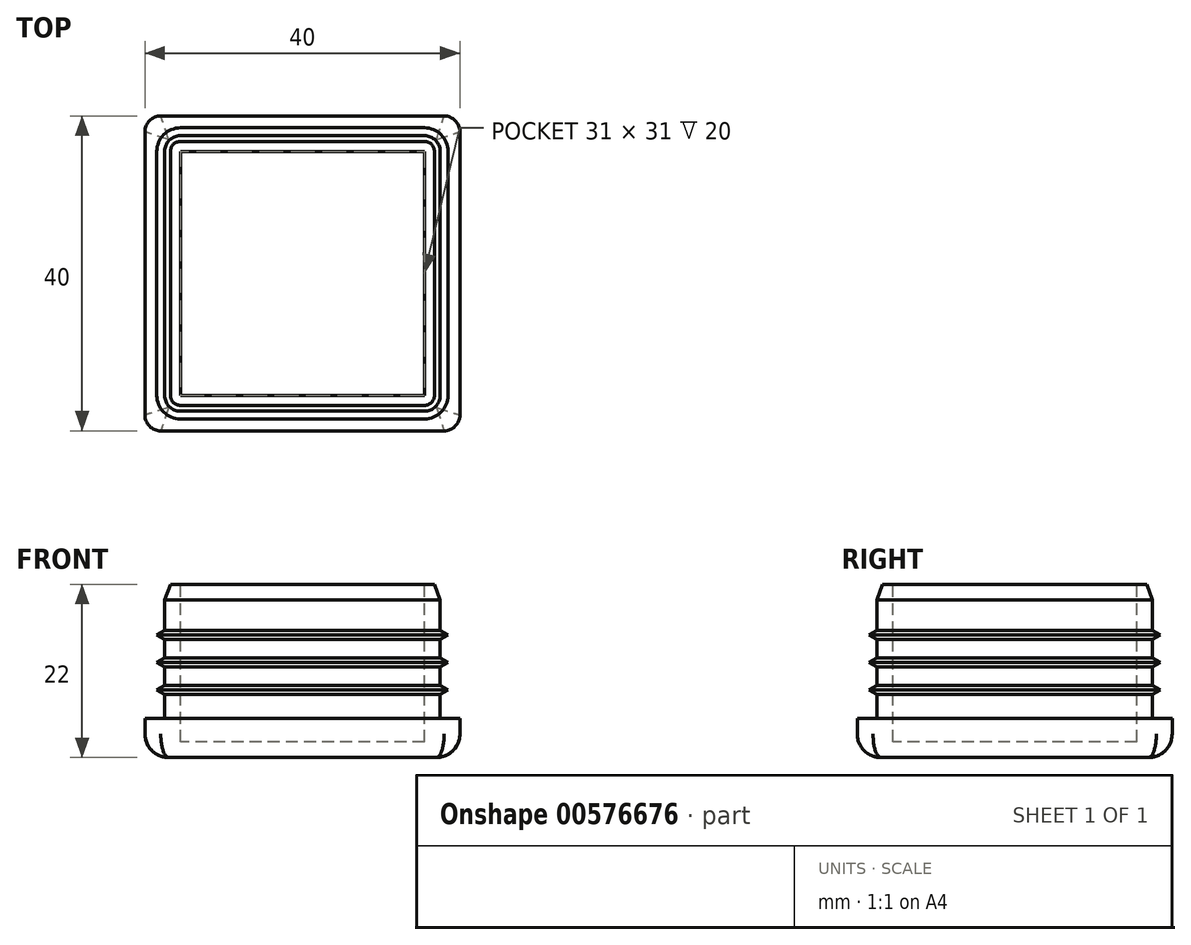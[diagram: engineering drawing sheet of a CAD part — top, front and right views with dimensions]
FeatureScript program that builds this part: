
annotation { "Feature Type Name" : "Feature", "Feature Type Description" : "" }
export const myFeature = defineFeature(function(context is Context, id is Id, definition is map)
    precondition{}
    {
        {
            var Q0;
            Q0=qCreatedBy(makeId("Top.planeOp"),FACE);
            var sketch = newSketch(context, id + "F0", { "sketchPlane" : qUnion([Q0])});
            skLineSegment(sketch, "E0.bottom", {"start": v(0, 0) * mm, "end": v(40, 0) * mm});
            skLineSegment(sketch, "E0.top", {"start": v(0, 40) * mm, "end": v(40, 40) * mm});
            skLineSegment(sketch, "E0.left", {"start": v(0, 0) * mm, "end": v(0, 40) * mm});
            skLineSegment(sketch, "E0.right", {"start": v(40, 0) * mm, "end": v(40, 40) * mm});
            skSolve(sketch);
        }
        {
            var Q0;
            Q0=makeQuery(id+"F0.imprint","IMPRINT",FACE,{"disambiguationData":[TD([[makeQuery(id+"F0.imprint","IMPRINT",EDGE,{"derivedFrom":sQuery(id+"F0.wireOp",EDGE,"E0.bottom")}),1.0]])]});
            extrude(context, id + "F1", {"entities" : qUnion([Q0]), "depth" : 5 * mm, "offsetDistance" : 25 * mm});
        }
        {
            var Q0;
            Q0=makeQuery(id+"F1.opExtrude","SWEPT_EDGE",EDGE,{"disambiguationData":[OSD([sQuery(id+"F0.wireOp",EDGE,"E0.bottom"),sQuery(id+"F0.wireOp",EDGE,"E0.left")])]});
            var Q1;
            Q1=makeQuery(id+"F1.opExtrude","SWEPT_EDGE",EDGE,{"disambiguationData":[OSD([sQuery(id+"F0.wireOp",EDGE,"E0.top"),sQuery(id+"F0.wireOp",EDGE,"E0.right")])]});
            var Q2;
            Q2=makeQuery(id+"F1.opExtrude","SWEPT_EDGE",EDGE,{"disambiguationData":[OSD([sQuery(id+"F0.wireOp",EDGE,"E0.bottom"),sQuery(id+"F0.wireOp",EDGE,"E0.right")])]});
            var Q3;
            Q3=makeQuery(id+"F1.opExtrude","SWEPT_EDGE",EDGE,{"disambiguationData":[OSD([sQuery(id+"F0.wireOp",EDGE,"E0.top"),sQuery(id+"F0.wireOp",EDGE,"E0.left")])]});
            fillet(context, id + "F2", {"entities" : qUnion([Q0, Q1, Q2, Q3]), "radius" : 2 * mm, "tangentPropagation" : true, "allowEdgeOverflow" : false});
        }
        {
            var Q0;
            Q0=makeQuery(id+"F1.opExtrude","CAP_FACE",FACE,{"disambiguationData":[OSD([sQuery(id+"F0.wireOp",EDGE,"E0.bottom"),sQuery(id+"F0.wireOp",EDGE,"E0.top"),sQuery(id+"F0.wireOp",EDGE,"E0.left"),sQuery(id+"F0.wireOp",EDGE,"E0.right")])],"isStart":true});
            fillet(context, id + "F3", {"entities" : qUnion([Q0]), "radius" : 3 * mm, "tangentPropagation" : true, "allowEdgeOverflow" : false});
        }
        {
            var Q0;
            Q0=makeQuery(id+"F1.opExtrude","CAP_FACE",FACE,{"disambiguationData":[OSD([sQuery(id+"F0.wireOp",EDGE,"E0.bottom"),sQuery(id+"F0.wireOp",EDGE,"E0.top"),sQuery(id+"F0.wireOp",EDGE,"E0.left"),sQuery(id+"F0.wireOp",EDGE,"E0.right")])],"isStart":false});
            var sketch = newSketch(context, id + "F4", { "sketchPlane" : qUnion([Q0])});
            skLineSegment(sketch, "E1.bottom", {"start": v(2.5, 37.5) * mm, "end": v(37.5, 37.5) * mm});
            skLineSegment(sketch, "E1.top", {"start": v(2.5, 2.5) * mm, "end": v(37.5, 2.5) * mm});
            skLineSegment(sketch, "E1.left", {"start": v(2.5, 37.5) * mm, "end": v(2.5, 2.5) * mm});
            skLineSegment(sketch, "E1.right", {"start": v(37.5, 37.5) * mm, "end": v(37.5, 2.5) * mm});
            skSolve(sketch);
        }
        {
            var Q0;
            Q0=makeQuery(id+"F4.imprint","IMPRINT",FACE,{"disambiguationData":[TD([[makeQuery(id+"F4.imprint","IMPRINT",EDGE,{"derivedFrom":sQuery(id+"F4.wireOp",EDGE,"E1.bottom")}),-1.0]])]});
            extrude(context, id + "F5", {"entities" : qUnion([Q0]), "operationType" : NewBodyOperationType.ADD, "depth" : 17 * mm, "offsetDistance" : 25 * mm});
        }
        {
            var Q0;
            Q0=makeQuery(id+"F5.opExtrude","SWEPT_EDGE",EDGE,{"disambiguationData":[OSD([sQuery(id+"F4.wireOp",EDGE,"E1.top"),sQuery(id+"F4.wireOp",EDGE,"E1.right")])]});
            var Q1;
            Q1=makeQuery(id+"F5.opExtrude","SWEPT_EDGE",EDGE,{"disambiguationData":[OSD([sQuery(id+"F4.wireOp",EDGE,"E1.bottom"),sQuery(id+"F4.wireOp",EDGE,"E1.right")])]});
            var Q2;
            Q2=makeQuery(id+"F5.opExtrude","SWEPT_EDGE",EDGE,{"disambiguationData":[OSD([sQuery(id+"F4.wireOp",EDGE,"E1.top"),sQuery(id+"F4.wireOp",EDGE,"E1.left")])]});
            var Q3;
            Q3=makeQuery(id+"F5.opExtrude","SWEPT_EDGE",EDGE,{"disambiguationData":[OSD([sQuery(id+"F4.wireOp",EDGE,"E1.bottom"),sQuery(id+"F4.wireOp",EDGE,"E1.left")])]});
            fillet(context, id + "F6", {"entities" : qUnion([Q0, Q1, Q2, Q3]), "radius" : 2 * mm, "tangentPropagation" : true, "allowEdgeOverflow" : false});
        }
        {
            var Q0;
            Q0=makeQuery(id+"F5.opExtrude","CAP_FACE",FACE,{"disambiguationData":[OSD([sQuery(id+"F4.wireOp",EDGE,"E1.bottom"),sQuery(id+"F4.wireOp",EDGE,"E1.top"),sQuery(id+"F4.wireOp",EDGE,"E1.left"),sQuery(id+"F4.wireOp",EDGE,"E1.right")])],"isStart":false});
            var sketch = newSketch(context, id + "F7", { "sketchPlane" : qUnion([Q0])});
            skLineSegment(sketch, "E2.bottom", {"start": v(4.5, 4.5) * mm, "end": v(35.5, 4.5) * mm});
            skLineSegment(sketch, "E2.top", {"start": v(4.5, 35.5) * mm, "end": v(35.5, 35.5) * mm});
            skLineSegment(sketch, "E2.left", {"start": v(4.5, 4.5) * mm, "end": v(4.5, 35.5) * mm});
            skLineSegment(sketch, "E2.right", {"start": v(35.5, 4.5) * mm, "end": v(35.5, 35.5) * mm});
            skSolve(sketch);
        }
        {
            var Q0;
            Q0=makeQuery(id+"F7.imprint","IMPRINT",FACE,{"disambiguationData":[TD([[makeQuery(id+"F7.imprint","IMPRINT",EDGE,{"derivedFrom":sQuery(id+"F7.wireOp",EDGE,"E2.bottom")}),1.0]])]});
            var Q1;
            Q1=makeQuery(id+"F1.opExtrude","CAP_FACE",FACE,{"disambiguationData":[OSD([sQuery(id+"F0.wireOp",EDGE,"E0.bottom"),sQuery(id+"F0.wireOp",EDGE,"E0.top"),sQuery(id+"F0.wireOp",EDGE,"E0.left"),sQuery(id+"F0.wireOp",EDGE,"E0.right")])],"isStart":true});
            extrude(context, id + "F8", {"entities" : qUnion([Q0]), "operationType" : NewBodyOperationType.REMOVE, "endBound" : BoundingType.UP_TO_SURFACE, "oppositeDirection" : true, "depth" : 20 * mm, "endBoundEntityFace" : qUnion([Q1]), "hasOffset" : true, "offsetDistance" : 2 * mm});
        }
        {
            var Q0;
            Q0=makeQuery(id+"F1.opExtrude","CAP_FACE",FACE,{"disambiguationData":[OSD([sQuery(id+"F0.wireOp",EDGE,"E0.bottom"),sQuery(id+"F0.wireOp",EDGE,"E0.top"),sQuery(id+"F0.wireOp",EDGE,"E0.left"),sQuery(id+"F0.wireOp",EDGE,"E0.right")])],"isStart":false});
            cPlane(context, id + "F9", {"entities" : qUnion([Q0]), "cplaneType" : CPlaneType.OFFSET, "offset" : 3 * mm, "width" : 150 * mm, "height" : 150 * mm});
        }
        {
            var Q0;
            Q0=qCreatedBy(id+"F9.planeOp",FACE);
            var sketch = newSketch(context, id + "F10", { "sketchPlane" : qUnion([Q0])});
            skLineSegment(sketch, "E3", {"start": v(37.5, 4.5) * mm, "end": v(37.5, 35.5) * mm});
            skArc(sketch, "E4", {"start": v(35.5, 2.5) * mm, "mid": v(36.91, 3.09) * mm, "end": v(37.5, 4.5) * mm});
            skLineSegment(sketch, "E5", {"start": v(35.5, 2.5) * mm, "end": v(4.5, 2.5) * mm});
            skLineSegment(sketch, "E6", {"start": v(2.5, 4.5) * mm, "end": v(2.5, 35.5) * mm});
            skArc(sketch, "E7", {"start": v(2.5, 4.5) * mm, "mid": v(3.09, 3.09) * mm, "end": v(4.5, 2.5) * mm});
            skArc(sketch, "E8", {"start": v(4.5, 37.5) * mm, "mid": v(3.09, 36.91) * mm, "end": v(2.5, 35.5) * mm});
            skLineSegment(sketch, "E9", {"start": v(35.5, 37.5) * mm, "end": v(4.5, 37.5) * mm});
            skArc(sketch, "E10", {"start": v(37.5, 35.5) * mm, "mid": v(36.91, 36.91) * mm, "end": v(35.5, 37.5) * mm});
            skSolve(sketch);
        }
        {
            var Q0;
            Q0=sQuery(id+"F10.wireOp",VERTEX,"E7.start");
            var Q1;
            Q1=qCreatedBy(makeId("Front.planeOp"),FACE);
            cPlane(context, id + "F11", {"entities" : qUnion([Q0, Q1]), "cplaneType" : CPlaneType.PLANE_POINT, "offset" : 25 * mm, "oppositeDirection" : true, "width" : 150 * mm, "height" : 150 * mm});
        }
        {
            var Q0;
            Q0=qCreatedBy(id+"F11.planeOp",FACE);
            var sketch = newSketch(context, id + "F12", { "sketchPlane" : qUnion([Q0])});
            skLineSegment(sketch, "E11", {"start": v(2.5, 16.15) * mm, "end": v(2.5, 22) * mm, "construction": true});
            skLineSegment(sketch, "E12", {"start": v(2.5, 8.58) * mm, "end": v(10.18, 8.58) * mm, "construction": true});
            skLineSegment(sketch, "E13.0", {"start": v(1.5, -0.73) * mm, "end": v(1.5, 8.58) * mm, "construction": true});
            skLineSegment(sketch, "E14", {"start": v(1.5, 8.58) * mm, "end": v(2.5, 9.15) * mm});
            skLineSegment(sketch, "E15", {"start": v(2.5, 9.15) * mm, "end": v(2.5, 8) * mm, "construction": true});
            skLineSegment(sketch, "E16", {"start": v(2.5, 8) * mm, "end": v(1.5, 8.58) * mm});
            skLineSegment(sketch, "E17.0.1.0", {"start": v(2.5, 11.5) * mm, "end": v(1.5, 12.08) * mm});
            skLineSegment(sketch, "E17.0.1.1", {"start": v(2.5, 12.65) * mm, "end": v(2.5, 11.5) * mm, "construction": true});
            skLineSegment(sketch, "E17.0.1.2", {"start": v(1.5, 12.08) * mm, "end": v(2.5, 12.65) * mm});
            skLineSegment(sketch, "E17.0.2.0", {"start": v(2.5, 15) * mm, "end": v(1.5, 15.58) * mm});
            skLineSegment(sketch, "E17.0.2.1", {"start": v(2.5, 16.15) * mm, "end": v(2.5, 15) * mm, "construction": true});
            skLineSegment(sketch, "E17.0.2.2", {"start": v(1.5, 15.58) * mm, "end": v(2.5, 16.15) * mm});
            skLineSegment(sketch, "E17.direction1", {"start": v(1.5, 8.58) * mm, "end": v(26.5, 8.58) * mm, "construction": true});
            skLineSegment(sketch, "E17.direction2", {"start": v(1.5, 8.58) * mm, "end": v(1.5, 12.08) * mm, "construction": true});
            skLineSegment(sketch, "E18", {"start": v(2.5, 16.15) * mm, "end": v(3, 16.15) * mm});
            skLineSegment(sketch, "E19", {"start": v(3, 16.15) * mm, "end": v(3, 8) * mm});
            skLineSegment(sketch, "E20", {"start": v(3, 8) * mm, "end": v(2.5, 8) * mm});
            skLineSegment(sketch, "E21", {"start": v(2.5, 9.15) * mm, "end": v(2.5, 11.5) * mm});
            skLineSegment(sketch, "E22", {"start": v(2.5, 12.65) * mm, "end": v(2.5, 15) * mm});
            skLineSegment(sketch, "E23.trimOffspring", {"start": v(2.5, 5) * mm, "end": v(2.5, 15) * mm, "construction": true});
            skSolve(sketch);
        }
        {
            var Q0;
            Q0=makeQuery(id+"F12.imprint","IMPRINT",FACE,{"disambiguationData":[TD([[makeQuery(id+"F12.imprint","IMPRINT",EDGE,{"derivedFrom":sQuery(id+"F12.wireOp",EDGE,"E14")}),-1.0]])]});
            var Q1;
            Q1=makeQuery(id+"F12.imprint","IMPRINT",FACE,{"disambiguationData":[TD([[makeQuery(id+"F12.imprint","IMPRINT",EDGE,{"derivedFrom":sQuery(id+"F12.wireOp",EDGE,"E17.0.1.0")}),-1.0]])]});
            var Q2;
            Q2=makeQuery(id+"F12.imprint","IMPRINT",FACE,{"disambiguationData":[TD([[makeQuery(id+"F12.imprint","IMPRINT",EDGE,{"derivedFrom":sQuery(id+"F12.wireOp",EDGE,"E17.0.2.0")}),-1.0]])]});
            var Q3;
            Q3=sQuery(id+"F10.wireOp",EDGE,"E6");
            var Q4;
            Q4=sQuery(id+"F10.wireOp",EDGE,"E8");
            var Q5;
            Q5=sQuery(id+"F10.wireOp",EDGE,"E9");
            var Q6;
            Q6=sQuery(id+"F10.wireOp",EDGE,"E10");
            var Q7;
            Q7=sQuery(id+"F10.wireOp",EDGE,"E3");
            var Q8;
            Q8=sQuery(id+"F10.wireOp",EDGE,"E4");
            var Q9;
            Q9=sQuery(id+"F10.wireOp",EDGE,"E5");
            var Q10;
            Q10=sQuery(id+"F10.wireOp",EDGE,"E7");
            sweep(context, id + "F13", {"operationType" : NewBodyOperationType.ADD, "profiles" : qUnion([Q0, Q1, Q2]), "path" : qUnion([Q3, Q4, Q5, Q6, Q7, Q8, Q9, Q10])});
        }
        {
            var Q0;
            Q0=makeQuery(id+"F5.opExtrude","CAP_EDGE",EDGE,{"disambiguationData":[OSD([sQuery(id+"F4.wireOp",EDGE,"E1.bottom")])],"isStart":false});
            chamfer(context, id + "F14", {"entities" : qUnion([Q0]), "chamferType" : ChamferType.OFFSET_ANGLE, "width" : 2 * mm, "oppositeDirection" : false, "angle" : 20 * degree, "tangentPropagation" : true});
        }
    });
